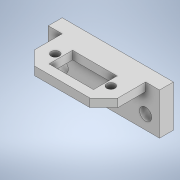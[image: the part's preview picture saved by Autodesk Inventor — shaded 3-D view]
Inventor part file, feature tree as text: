
AUTODESK INVENTOR PART (.ipt)
format: ipt  version: 2022 (Build 260153000, 153)  size: 147,968 bytes
history: native  units: mm
features: extrude x3, sketch x3, chamfer x1
ambient origin geometry x8: Origin, YZ Plane, XZ Plane, XY Plane, X Axis, Y Axis, Z Axis, Center Point
bodies: Solid1 (feature_tree)
feature tree (7):
  extrude  "Extrusion1"  Depth=15.0mm
  extrude  "Extrusion2"  Depth=8.5mm
  extrude  "Extrusion3"  Depth=3.25mm
  chamfer  "Chamfer1"  Distance=3.0mm
  sketch  "Sketch1"  dims[d0=40.0mm d1=15.0mm]
  sketch  "Sketch2"  dims[d2=5.0mm d3=0.0mm d4=8.5mm]
  sketch  "Sketch3"  dims[d7=4.25mm d8=4.25mm d9=3.0mm d10=3.0mm d11=20.0mm d13=16.0mm d14=2.0mm d15=3.0mm d16=0.0mm d17=4.4mm d18=5.0mm d19=5.0mm d20=4.4mm d21=5.0mm d22=5.0mm d23=10.0mm d24=0.0mm d25=5.0mm d26=2.0mm d27=45.0deg d28=5.0mm d29=5.0mm d30=5.0mm d31=15.0mm d32=3.25mm]
